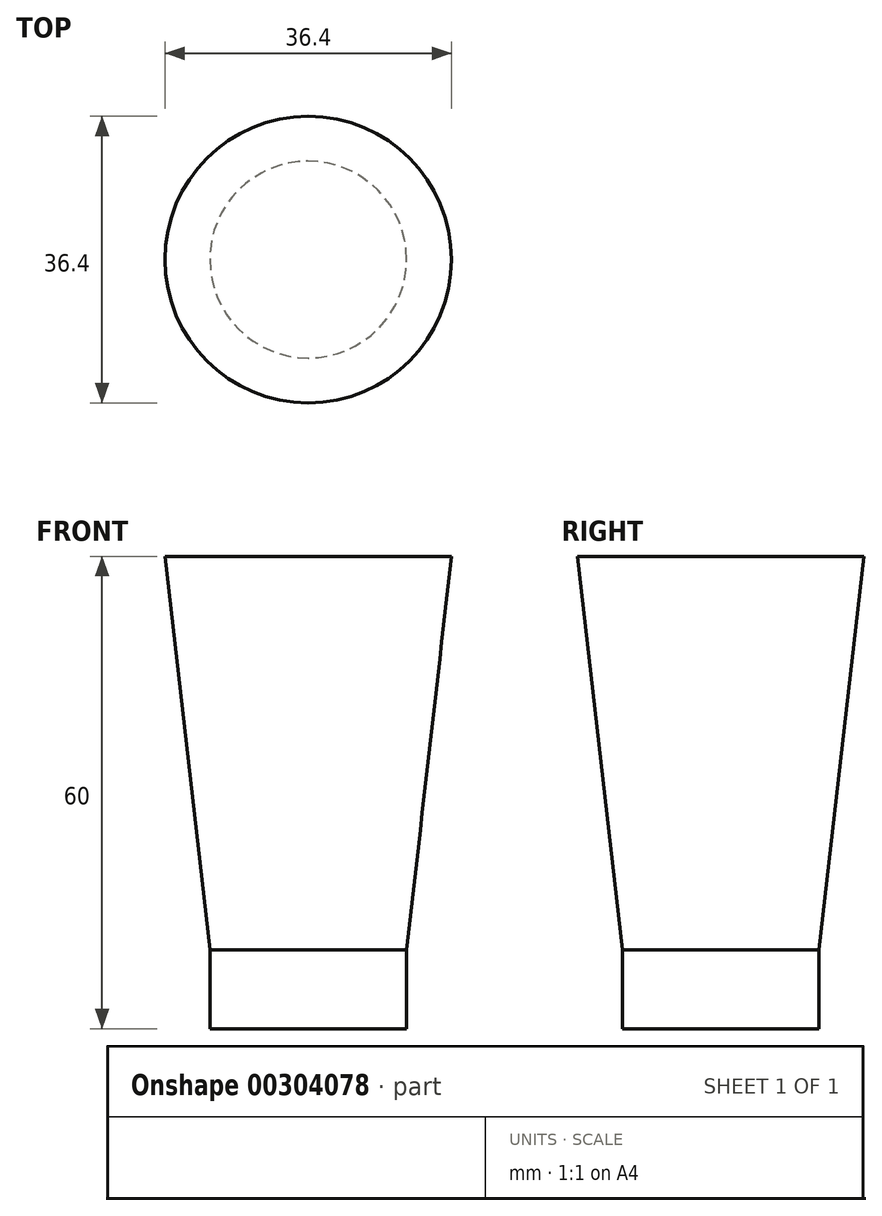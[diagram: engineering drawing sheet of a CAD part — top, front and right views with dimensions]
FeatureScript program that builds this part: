
annotation { "Feature Type Name" : "Feature", "Feature Type Description" : "" }
export const myFeature = defineFeature(function(context is Context, id is Id, definition is map)
    precondition{}
    {
        {
            var Q0;
            Q0=qCreatedBy(makeId("Top.planeOp"),FACE);
            var sketch = newSketch(context, id + "F0", { "sketchPlane" : qUnion([Q0])});
            skCircle(sketch, "E0", {"center": v(0, 0) * mm, "radius": 12.5 * mm});
            skSolve(sketch);
        }
        {
            var Q0;
            Q0=makeQuery(id+"F0.imprint","IMPRINT",FACE,{"disambiguationData":[TD([[makeQuery(id+"F0.imprint","IMPRINT",EDGE,{"derivedFrom":sQuery(id+"F0.wireOp",EDGE,"E0")}),1.0]])]});
            extrude(context, id + "F1", {"entities" : qUnion([Q0]), "depth" : 50 * mm, "hasDraft" : true, "draftAngle" : 6.5 * degree, "hasSecondDirection" : true, "secondDirectionOppositeDirection" : true, "secondDirectionDepth" : 10 * mm});
        }
    });
